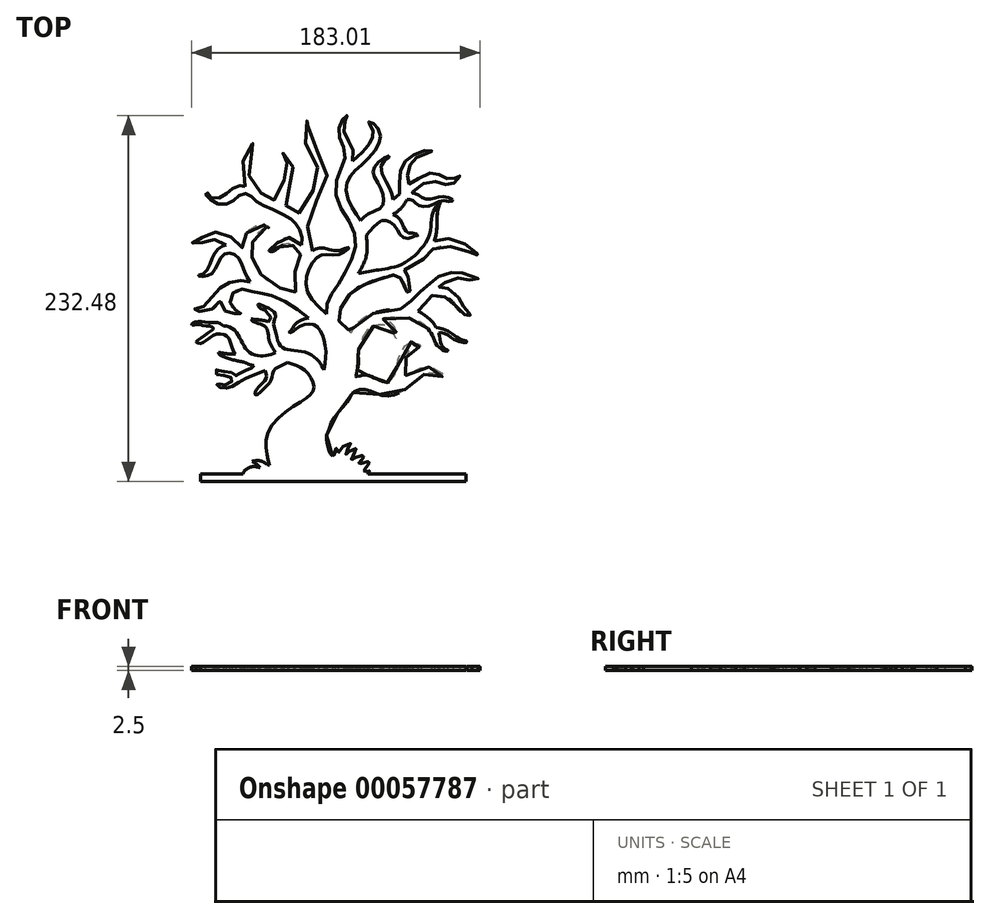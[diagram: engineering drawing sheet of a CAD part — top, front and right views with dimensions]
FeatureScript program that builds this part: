
annotation { "Feature Type Name" : "Feature", "Feature Type Description" : "" }
export const myFeature = defineFeature(function(context is Context, id is Id, definition is map)
    precondition{}
    {
        {
            var Q0;
            Q0=qCreatedBy(makeId("Top.planeOp"),FACE);
            var sketch = newSketch(context, id + "F0", { "sketchPlane" : qUnion([Q0])});
            skFitSpline(sketch, "E0", {"points": [v(-37.23, -92.22) * mm, v(-37.93, -89.5) * mm, v(-37.64, -70.07) * mm, v(-14, -49.38) * mm, v(-9.05, -42.86) * mm, v(-12.92, -33.47) * mm, v(-20.4, -28.62) * mm, v(-30.52, -26.33) * mm, v(-44.65, -28.9) * mm, v(-53.5, -26.46) * mm], "startDerivative": vector(-6.46, 28.02) * mm, "endDerivative": vector(-86.12, 39.68) * mm});
            skFitSpline(sketch, "E1", {"points": [v(-53.5, -26.46) * mm, v(-62.24, -24.53) * mm, v(-69.12, -21.43) * mm, v(-69.55, -20.32) * mm], "startDerivative": vector(-17.56, 2.77) * mm, "endDerivative": vector(-0.49, 6.57) * mm});
            skFitSpline(sketch, "E2", {"points": [v(-69.55, -20.32) * mm, v(-63.18, -21.35) * mm, v(-58.8, -21.52) * mm], "startDerivative": vector(12.15, -2.3) * mm, "endDerivative": vector(9.28, -0.04) * mm});
            skFitSpline(sketch, "E3", {"points": [v(-58.8, -21.52) * mm, v(-61.03, -17.47) * mm, v(-63.61, -10.67) * mm, v(-71.93, -9.08) * mm, v(-80.86, -14.69) * mm, v(-83.78, -13.74) * mm, v(-82.12, -12.32) * mm, v(-68.6, -3.79) * mm, v(-58.2, -7.58) * mm, v(-51.73, -18.6) * mm, v(-42.1, -22.64) * mm, v(-33.23, -20.57) * mm], "startDerivative": vector(-32.51, 46.9) * mm, "endDerivative": vector(77.44, 28.59) * mm});
            skFitSpline(sketch, "E4", {"points": [v(-33.23, -20.57) * mm, v(-37.27, -13.17) * mm, v(-39.86, -4.05) * mm, v(-47.76, -0.64) * mm, v(-48.83, 0.83) * mm], "startDerivative": vector(-16.8, 23.88) * mm, "endDerivative": vector(0.64, 6.3) * mm});
            skFitSpline(sketch, "E5", {"points": [v(-48.83, 0.83) * mm, v(-35.48, -2.55) * mm, v(-31.57, -14.02) * mm, v(-26.34, -18.5) * mm, v(-14.47, -20.28) * mm, v(-5.83, -26.09) * mm, v(-2.67, -31.48) * mm], "startDerivative": vector(73.32, -8.54) * mm, "endDerivative": vector(18.96, -39.09) * mm});
            skFitSpline(sketch, "E6", {"points": [v(-2.67, -31.48) * mm, v(-1.43, -19.6) * mm, v(-3.36, -10.05) * mm, v(-7.1, -3.92) * mm, v(-12.97, -2.37) * mm, v(-19.74, -4.89) * mm, v(-22.7, -7.34) * mm, v(-24.45, -7.73) * mm, v(-24.64, -7.2) * mm, v(-23.41, -6.37) * mm, v(-21.54, -3.28) * mm, v(-17.68, 0) * mm, v(-12.52, 1.37) * mm], "startDerivative": vector(16.4, 90.94) * mm, "endDerivative": vector(60.2, 10.33) * mm});
            skFitSpline(sketch, "E7", {"points": [v(-12.52, 1.37) * mm, v(-24.06, 10) * mm, v(-38, 16.41) * mm, v(-45.65, 17.78) * mm, v(-49.75, 18.87) * mm, v(-57.81, 19.42) * mm, v(-62.18, 13.68) * mm, v(-60.95, 8.35) * mm, v(-56.05, 5.43) * mm, v(-55.53, 4.23) * mm, v(-58.2, 4.23) * mm, v(-64.66, 5.34) * mm, v(-68.36, 11.89) * mm, v(-68.7, 12.49) * mm, v(-69.22, 12.32) * mm, v(-70.43, 10) * mm, v(-78.6, 5.6) * mm, v(-84.97, 6.9) * mm, v(-84.8, 7.24) * mm, v(-79.3, 8.79) * mm, v(-71.63, 17.4) * mm, v(-65, 22.99) * mm, v(-55.7, 25.14) * mm, v(-49.5, 24.45) * mm], "startDerivative": vector(-156.26, 128.1) * mm, "endDerivative": vector(126.07, -24.69) * mm});
            skFitSpline(sketch, "E8", {"points": [v(-49.5, 24.45) * mm, v(-52.85, 30.29) * mm, v(-56.83, 39.4) * mm, v(-61.9, 42.67) * mm, v(-66.9, 41.22) * mm, v(-70.51, 35) * mm, v(-73.99, 29.64) * mm, v(-78.7, 28.05) * mm, v(-82.24, 28.19) * mm, v(-82.31, 28.62) * mm, v(-81.95, 28.7) * mm, v(-78.9, 29.64) * mm, v(-74.78, 36.15) * mm, v(-72.25, 42.38) * mm, v(-67.83, 46.86) * mm, v(-64.72, 47.95) * mm], "startDerivative": vector(-43.88, 65.41) * mm, "endDerivative": vector(53.78, 11.6) * mm});
            skFitSpline(sketch, "E9", {"points": [v(-64.72, 47.95) * mm, v(-68.7, 50.12) * mm, v(-73.4, 51.28) * mm, v(-78.33, 50.27) * mm, v(-80.5, 49.18) * mm, v(-85.35, 48.96) * mm, v(-86.07, 49.1) * mm, v(-85.78, 49.61) * mm, v(-82.89, 50.92) * mm, v(-78.62, 53.81) * mm, v(-72.9, 55.91) * mm, v(-65.52, 54.75) * mm, v(-59.37, 50.84) * mm, v(-54.73, 46.28) * mm, v(-54.3, 46.5) * mm, v(-52.49, 53.96) * mm, v(-44.31, 60.4) * mm, v(-37.43, 59.68) * mm, v(-37.65, 59.1) * mm, v(-38.8, 59.24) * mm, v(-46.4, 53.02) * mm, v(-48.65, 44.48) * mm, v(-47.93, 38.47) * mm, v(-42.28, 28.99) * mm, v(-29.9, 20.37) * mm, v(-20.79, 17.84) * mm, v(-20.71, 18.06) * mm, v(-21.3, 28.26) * mm, v(-18.04, 39.84) * mm, v(-17.75, 42.6) * mm, v(-19.77, 45.63) * mm, v(-25.27, 48.67) * mm, v(-30.85, 46.65) * mm, v(-35.26, 43.75) * mm, v(-37.43, 44.19) * mm, v(-37.22, 44.55) * mm, v(-35.77, 45.34) * mm, v(-31.43, 50.34) * mm, v(-27.23, 52.58) * mm, v(-21.44, 51.71) * mm, v(-16.73, 47.95) * mm], "startDerivative": vector(-159.85, 95.28) * mm, "endDerivative": vector(153.51, -155.1) * mm});
            skFitSpline(sketch, "E10", {"points": [v(-16.73, 47.95) * mm, v(-16.73, 53.67) * mm, v(-19.41, 59.82) * mm, v(-21.8, 62.93) * mm, v(-27.3, 66.7) * mm, v(-38.3, 71.84) * mm, v(-45.4, 75.53) * mm, v(-48.58, 78.71) * mm, v(-52.78, 80.67) * mm, v(-57.48, 78.57) * mm, v(-61.97, 74.88) * mm, v(-68.63, 73.57) * mm, v(-75.36, 77.2) * mm, v(-77.68, 80.45) * mm, v(-76.66, 81.24) * mm, v(-76.45, 80.23) * mm, v(-72.76, 77.34) * mm, v(-65.37, 79.87) * mm, v(-60.52, 83.78) * mm, v(-54.95, 85.59) * mm, v(-52.63, 85.08) * mm], "startDerivative": vector(12.24, 106.84) * mm, "endDerivative": vector(59.66, -23.4) * mm});
            skFitSpline(sketch, "E11", {"points": [v(-52.63, 85.08) * mm, v(-54.59, 91.38) * mm, v(-53.72, 102.23) * mm, v(-50.25, 108.9) * mm, v(-47.86, 112) * mm, v(-47.86, 112.8) * mm, v(-47.5, 113.45) * mm, v(-46.63, 113.02) * mm, v(-46.77, 111.14) * mm, v(-47.93, 109.11) * mm, v(-50.25, 102.3) * mm, v(-50.17, 92.1) * mm, v(-47.06, 85.66) * mm, v(-42.72, 81.24) * mm, v(-41.78, 79.8) * mm, v(-35.77, 76.25) * mm, v(-34.32, 75.82) * mm, v(-34.25, 76.76) * mm, v(-31.79, 83.42) * mm, v(-28.17, 88.34) * mm, v(-25.27, 93.33) * mm, v(-25.2, 98.1) * mm, v(-27.23, 101.87) * mm, v(-29.11, 103.9) * mm, v(-29.62, 105.78) * mm, v(-29.26, 106.43) * mm, v(-28.53, 105.85) * mm, v(-28.82, 104.91) * mm, v(-26.72, 103.25) * mm, v(-22.16, 96.73) * mm, v(-21.94, 90) * mm, v(-24.7, 83.92) * mm, v(-27.37, 78.35) * mm, v(-27.37, 74.15) * mm, v(-26.65, 72.63) * mm, v(-22.81, 70.39) * mm, v(-18.76, 67.28) * mm, v(-18.69, 67.64) * mm, v(-12.97, 78.06) * mm, v(-9.93, 81.9) * mm, v(-6.38, 90) * mm, v(-6.31, 96.52) * mm, v(-11.09, 106) * mm, v(-14.63, 113.53) * mm, v(-15.5, 119.39) * mm, v(-13.4, 126.92) * mm, v(-11.81, 128.94) * mm, v(-11.23, 128.3) * mm, v(-11.74, 127.57) * mm, v(-12.82, 122) * mm, v(-10.44, 113.67) * mm, v(-5.3, 105.5) * mm, v(-1.03, 98.04) * mm, v(-1.53, 85.73) * mm, v(-5.95, 77.84) * mm, v(-12.32, 68.8) * mm, v(-12.82, 59.39) * mm, v(-10.87, 56.42) * mm, v(-9.93, 44.19) * mm], "startDerivative": vector(-120.08, 280.65) * mm, "endDerivative": vector(-5.28, -540.47) * mm});
            skFitSpline(sketch, "E12", {"points": [v(-9.93, 44.19) * mm, v(-7.69, 45.56) * mm, v(-3.85, 46.07) * mm, v(1.36, 44.9) * mm, v(7, 44.19) * mm, v(12.36, 46.21) * mm, v(13.3, 46.14) * mm, v(11.57, 44.19) * mm, v(5.7, 41.5) * mm, v(-2.26, 41.8) * mm, v(-7.18, 39.77) * mm, v(-12.68, 31.01) * mm, v(-13.26, 18.64) * mm, v(-1.03, 4.16) * mm], "startDerivative": vector(40.45, 30.37) * mm, "endDerivative": vector(114.16, -103.83) * mm});
            skFitSpline(sketch, "E13", {"points": [v(-1.03, 4.16) * mm, v(0, 12.2) * mm, v(5.27, 20.94) * mm, v(12.32, 33.52) * mm, v(17.54, 48.24) * mm, v(14.16, 61.43) * mm, v(5.88, 76.46) * mm, v(6.19, 92.1) * mm, v(10.8, 102.53) * mm, v(9.1, 112.04) * mm, v(6.65, 119.25) * mm, v(8.34, 126.15) * mm, v(10.94, 129.83) * mm, v(12.17, 129.99) * mm, v(10.8, 126.15) * mm, v(10.94, 117.72) * mm, v(15.24, 110.2) * mm, v(15.54, 101.3) * mm], "startDerivative": vector(2.52, 146.68) * mm, "endDerivative": vector(-17.17, -159.84) * mm});
            skFitSpline(sketch, "E14", {"points": [v(15.54, 101.3) * mm, v(20.45, 105.45) * mm, v(23.52, 108.67) * mm, v(27.05, 113.73) * mm, v(28.43, 120.94) * mm, v(25.97, 125.08) * mm, v(25.97, 126) * mm, v(29.8, 124.31) * mm, v(33.18, 117.1) * mm, v(29.96, 108.05) * mm, v(20, 97.62) * mm, v(13.86, 91.18) * mm, v(11.25, 83.36) * mm, v(15.54, 71.25) * mm, v(20.76, 63.27) * mm], "startDerivative": vector(77.02, 62.47) * mm, "endDerivative": vector(65.04, -83.73) * mm});
            skFitSpline(sketch, "E15", {"points": [v(20.76, 63.27) * mm, v(25.05, 67.26) * mm, v(33.95, 71.86) * mm, v(35.33, 76.61) * mm, v(33.34, 84.44) * mm, v(28.58, 93.33) * mm, v(31.19, 99.47) * mm, v(38.24, 104.37) * mm, v(39.01, 103.91) * mm, v(33.8, 98.85) * mm, v(38.86, 84.44) * mm, v(41.16, 76.61) * mm], "startDerivative": vector(41.17, 51.56) * mm, "endDerivative": vector(11.33, -71.84) * mm});
            skFitSpline(sketch, "E16", {"points": [v(41.16, 76.61) * mm, v(45.45, 80.6) * mm, v(45.29, 90.93) * mm, v(48.66, 100.29) * mm, v(54.18, 105.04) * mm, v(63.67, 108.12) * mm, v(65.97, 107.5) * mm, v(65.66, 107.04) * mm, v(59.09, 104.9) * mm, v(52.95, 99.98) * mm, v(50.5, 92.31) * mm, v(51.6, 86.62) * mm, v(60.83, 92.2) * mm, v(68.8, 93.27) * mm, v(74.16, 90.66) * mm, v(79.38, 89.9) * mm, v(83.36, 92.2) * mm, v(83.67, 91.89) * mm, v(79.68, 86.98) * mm, v(73.7, 86.37) * mm, v(64.96, 88.51) * mm, v(53.89, 81.83) * mm, v(50.2, 76.61) * mm, v(45.76, 70.63) * mm, v(41.16, 67.26) * mm], "startDerivative": vector(110.78, 80.65) * mm, "endDerivative": vector(-110.46, -69.26) * mm});
            skFitSpline(sketch, "E17", {"points": [v(41.16, 67.26) * mm, v(45.24, 64.63) * mm, v(47.07, 61.26) * mm, v(49.26, 57.16) * mm, v(51.45, 55.51) * mm, v(55.55, 55.33) * mm, v(57, 53.78) * mm, v(56.37, 53.6) * mm, v(55.28, 53.7) * mm, v(50.9, 52.05) * mm, v(46.89, 53.33) * mm, v(42.96, 59.07) * mm, v(38.4, 63.08) * mm, v(34.03, 63.27) * mm, v(28.92, 59.25) * mm, v(24.36, 54.06) * mm], "startDerivative": vector(63.37, -31.9) * mm, "endDerivative": vector(-49.93, -59.23) * mm});
            skFitSpline(sketch, "E18", {"points": [v(24.36, 54.06) * mm, v(24.36, 41.38) * mm, v(19.25, 29.8) * mm], "startDerivative": vector(2.56, -25.89) * mm, "endDerivative": vector(-12.77, -22.63) * mm});
            skFitSpline(sketch, "E19", {"points": [v(19.25, 29.8) * mm, v(27.1, 31.26) * mm, v(35.21, 32.53) * mm, v(48.07, 36.27) * mm, v(61.84, 49.13) * mm, v(65.3, 59.07) * mm, v(66.22, 67.19) * mm, v(70.78, 74.76) * mm, v(71.14, 74.76) * mm, v(69.96, 71.47) * mm, v(69.14, 61.17) * mm, v(68.68, 54.97) * mm, v(67.5, 50.32) * mm], "startDerivative": vector(92.84, 17.97) * mm, "endDerivative": vector(-20.5, -69.36) * mm});
            skFitSpline(sketch, "E20", {"points": [v(67.5, 50.32) * mm, v(73.24, 51.87) * mm, v(83.73, 50.32) * mm, v(89.93, 45.85) * mm, v(95.13, 42.66) * mm, v(96.22, 42.38) * mm, v(96.22, 41.65) * mm, v(94.76, 41.56) * mm, v(94.58, 40.92) * mm, v(93.21, 41.47) * mm, v(84.73, 45.4) * mm, v(71.05, 46.76) * mm, v(64.94, 44.02) * mm, v(60.66, 38.92) * mm, v(48.17, 31.66) * mm, v(47.97, 31.21) * mm, v(49.1, 30.12) * mm, v(51.78, 24.65) * mm, v(52.02, 18.07) * mm, v(51.94, 16.29) * mm, v(50.88, 16.45) * mm, v(49.18, 23.11) * mm, v(44.38, 27.82) * mm, v(42.27, 28.31) * mm, v(41.78, 28.72) * mm, v(39.35, 28.15) * mm, v(28.54, 24.98) * mm, v(21.96, 22.14) * mm, v(13.75, 16.53) * mm, v(8.47, 8.57) * mm, v(6.93, 3.45) * mm, v(7.25, -1.34) * mm, v(12.21, -5.16) * mm, v(14.4, -7.84) * mm, v(14.9, -7.36) * mm, v(22.37, 1.34) * mm, v(46.09, 7.27) * mm], "startDerivative": vector(168, 66.2) * mm, "endDerivative": vector(398.56, 17.42) * mm});
            skFitSpline(sketch, "E21", {"points": [v(46.09, 7.27) * mm, v(52.9, 12.63) * mm, v(59.47, 18.84) * mm, v(65.07, 23.59) * mm, v(69.81, 27.6) * mm, v(78.33, 30.4) * mm, v(84.54, 30.04) * mm, v(89.05, 29.07) * mm, v(92.58, 27.24) * mm, v(95.25, 26.75) * mm, v(94.65, 25.78) * mm, v(88.56, 26.02) * mm, v(82.1, 26.88) * mm, v(73.22, 23.59) * mm, v(70.79, 22.14) * mm, v(70.66, 21.03) * mm, v(75.05, 20.67) * mm, v(82.47, 14.95) * mm, v(85.64, 9.71) * mm, v(87.34, 6.91) * mm, v(90.26, 4.33) * mm, v(91.36, 4.33) * mm, v(90.38, 3.26) * mm, v(89.17, 2.65) * mm, v(87.34, 3.14) * mm, v(82.72, 6.91) * mm, v(76.26, 13.97) * mm, v(66.65, 15.92) * mm, v(64.94, 15.19) * mm, v(58.86, 7.27) * mm, v(57.15, 5.94) * mm], "startDerivative": vector(152.87, 113.18) * mm, "endDerivative": vector(-62.21, -32.26) * mm});
            skFitSpline(sketch, "E22", {"points": [v(57.15, 5.94) * mm, v(61.99, 2.85) * mm, v(67.5, -2.44) * mm, v(68.41, -4.26) * mm, v(71.56, -5.08) * mm, v(78.86, -8.46) * mm, v(84.92, -12.6) * mm, v(88.02, -13.15) * mm, v(88.02, -13.88) * mm, v(86.47, -14.2) * mm, v(79.81, -12.1) * mm, v(76.17, -9.41) * mm, v(71.74, -7.77) * mm, v(70.33, -8.1) * mm, v(70.33, -8.46) * mm, v(71.56, -14.02) * mm, v(73.34, -17.4) * mm, v(75.94, -18.94) * mm, v(76.08, -19.3) * mm, v(74.89, -19.63) * mm, v(72.56, -18.62) * mm, v(68.6, -14.93) * mm, v(66.32, -9.78) * mm, v(63.44, -5.31) * mm, v(59.66, -1.9) * mm, v(52.55, 1.2) * mm, v(39.76, 1.72) * mm, v(35.05, 1) * mm, v(39.45, -1.25) * mm, v(42.21, -4.94) * mm, v(43.75, -9.95) * mm, v(43.24, -11.59) * mm, v(42.72, -11.18) * mm, v(42.72, -10.26) * mm, v(37.5, -3.91) * mm, v(32.08, -2.89) * mm, v(25.32, -5.86) * mm, v(19.7, -17.12) * mm, v(19.18, -22.95) * mm, v(19.28, -27.56) * mm, v(17.65, -35.13) * mm, v(17.54, -35.75) * mm, v(23.38, -34.72) * mm, v(29.21, -36.57) * mm, v(35.87, -39.12) * mm, v(39.04, -39.02) * mm, v(43.34, -32.68) * mm, v(43.65, -30.22) * mm, v(47.33, -17.83) * mm, v(54.3, -13.43) * mm, v(57.62, -15.17) * mm, v(59.4, -16.4) * mm, v(57.62, -16.8) * mm, v(54.8, -16.3) * mm, v(50.5, -20.4) * mm, v(49.28, -28.48) * mm, v(49.38, -33.29) * mm, v(49.17, -34.93) * mm, v(50.7, -34.21) * mm, v(60.23, -29.8) * mm, v(70.67, -32.27) * mm, v(73.74, -35.75) * mm, v(72.61, -35.75) * mm, v(69.65, -34.1) * mm, v(63.1, -33.7) * mm, v(58.8, -35.64) * mm, v(51.63, -41.89) * mm, v(45.9, -45.78) * mm, v(35.35, -47.93) * mm, v(23.79, -43.83) * mm, v(15.5, -46.29) * mm, v(12.53, -51.2) * mm, v(3.72, -62.16) * mm, v(0, -70.45) * mm, v(-0.97, -74.78) * mm, v(1.22, -84.1) * mm, v(2.74, -86.23) * mm], "startDerivative": vector(316.06, -183.06) * mm, "endDerivative": vector(154.23, -155.5) * mm});
            skFitSpline(sketch, "E23", {"points": [v(-37.23, -92.22) * mm, v(-42.9, -89.27) * mm, v(-48.15, -89.53) * mm], "startDerivative": vector(-10.66, 5.99) * mm, "endDerivative": vector(-10.92, -1.79) * mm});
            skFitSpline(sketch, "E24", {"points": [v(-48.15, -89.53) * mm, v(-44.28, -92.2) * mm, v(-43.24, -93.49) * mm], "startDerivative": vector(7.24, -4.5) * mm, "endDerivative": vector(2.14, -3.32) * mm});
            skFitSpline(sketch, "E25", {"points": [v(-43.24, -93.49) * mm, v(-48.32, -93.02) * mm, v(-53.03, -95.51) * mm, v(-53.92, -97.56) * mm], "startDerivative": vector(-13.25, 3.2) * mm, "endDerivative": vector(-1.8, -8.27) * mm});
            skFitSpline(sketch, "E26", {"points": [v(-53.92, -97.56) * mm, v(-51.05, -96.88) * mm, v(-46.37, -97.56) * mm], "startDerivative": vector(6.09, 2.16) * mm, "endDerivative": vector(8.9, -2) * mm});
            skLineSegment(sketch, "E27", {"start": v(-46.37, -97.56) * mm, "end": v(-46.37, -97.56) * mm});
            skLineSegment(sketch, "E28", {"start": v(-84.8, 7.24) * mm, "end": v(-85.32, 24.31) * mm, "construction": true});
            skLineSegment(sketch, "E29", {"start": v(-85.32, 24.31) * mm, "end": v(91.36, 4.33) * mm, "construction": true});
            skFitSpline(sketch, "E30", {"points": [v(70.33, -8.1) * mm, v(68.72, -8.1) * mm, v(66.26, -7.43) * mm, v(63.44, -5.31) * mm], "startDerivative": vector(-5.7, -0.28) * mm, "endDerivative": vector(-6.95, 6.19) * mm});
            skFitSpline(sketch, "E31", {"points": [v(-34.41, -4.06) * mm, v(-34.29, 0) * mm, v(-33.2, 2.67) * mm, v(-35.78, 6.6) * mm, v(-41.56, 9.35) * mm, v(-44.25, 10.34) * mm, v(-44.5, 10) * mm, v(-43.16, 7.66) * mm, v(-39.92, 6.36) * mm, v(-38.47, 4.42) * mm, v(-36.48, 1.98) * mm, v(-37.97, -0.91) * mm], "startDerivative": vector(-4.06, 42.22) * mm, "endDerivative": vector(-27.8, -32.84) * mm});
            skFitSpline(sketch, "E32", {"points": [v(-66.39, -3.5) * mm, v(-69.47, -1.64) * mm, v(-75.72, -1.33) * mm, v(-83.78, -0.85) * mm, v(-86.63, -2.43) * mm, v(-86.16, -2.9) * mm, v(-82.76, -2.51) * mm, v(-79.75, -3.15) * mm, v(-73.11, -4.41) * mm, v(-73.18, -5.8) * mm], "startDerivative": vector(-25.1, 20.7) * mm, "endDerivative": vector(-9.63, -22.76) * mm});
            skFitSpline(sketch, "E33", {"points": [v(-28.41, -26.35) * mm, v(-37.58, -30.63) * mm, v(-44.34, -33.71) * mm, v(-52.48, -37.04) * mm, v(-60.53, -41.8) * mm, v(-66.41, -43.07) * mm, v(-70.63, -41.1) * mm, v(-69.94, -40.13) * mm, v(-67.5, -41.1) * mm, v(-60.83, -38.27) * mm, v(-63.57, -35.23) * mm, v(-71.2, -33.79) * mm, v(-70.33, -30.85) * mm, v(-69.25, -32.02) * mm, v(-61.9, -32.87) * mm, v(-58.08, -35.13) * mm, v(-54.83, -32.73) * mm, v(-48.07, -30.18) * mm, v(-46.87, -28.77) * mm], "startDerivative": vector(-105.13, -29.15) * mm, "endDerivative": vector(29.74, 40.47) * mm});
            skLineSegment(sketch, "E34", {"start": v(25.38, -97.56) * mm, "end": v(87.75, -97.56) * mm});
            skLineSegment(sketch, "E35", {"start": v(87.75, -97.56) * mm, "end": v(87.75, -102.35) * mm});
            skLineSegment(sketch, "E36", {"start": v(87.75, -102.35) * mm, "end": v(-81.07, -102.35) * mm});
            skLineSegment(sketch, "E37", {"start": v(-81.07, -102.35) * mm, "end": v(-81.07, -97.56) * mm});
            skLineSegment(sketch, "E38", {"start": v(-81.07, -97.56) * mm, "end": v(-46.37, -97.56) * mm});
            skFitSpline(sketch, "E39", {"points": [v(2.74, -86.23) * mm, v(3.57, -86.66) * mm, v(4.11, -84.1) * mm, v(5.53, -80.54) * mm, v(5.63, -81.32) * mm, v(6.37, -84.1) * mm, v(8.42, -81.08) * mm, v(14.45, -78.38) * mm, v(12.3, -81.57) * mm, v(11.41, -85.24) * mm, v(13.96, -82.74) * mm, v(18.08, -81.57) * mm, v(16.17, -84.8) * mm, v(14.85, -88.77) * mm, v(18.23, -86.23) * mm, v(23.08, -86.23) * mm, v(20.82, -88.53) * mm, v(19.45, -91.56) * mm, v(23.18, -90.04) * mm, v(26.7, -90.2) * mm, v(24.06, -93.08) * mm, v(22.74, -96.42) * mm, v(24.16, -95.63) * mm, v(26.17, -95.48) * mm, v(25.48, -96.8) * mm, v(25.38, -97.56) * mm], "startDerivative": vector(43.65, -35.45) * mm, "endDerivative": vector(4.37, -33.58) * mm});
            skFitSpline(sketch, "E40", {"points": [v(-25.76, -26.76) * mm, v(-31, -29.27) * mm, v(-34.93, -32.5) * mm, v(-35.97, -37.6) * mm, v(-39.9, -42.45) * mm, v(-45.8, -47.53) * mm, v(-45.91, -44.88) * mm, v(-40.83, -38.98) * mm, v(-39.2, -35.86) * mm, v(-39.98, -31.83) * mm], "startDerivative": vector(-45.07, -20.48) * mm, "endDerivative": vector(-15.86, 43.29) * mm});
            skFitSpline(sketch, "E41", {"points": [v(61.84, 49.13) * mm, v(65.02, 50.52) * mm, v(67.5, 50.32) * mm], "startDerivative": vector(6, 3.37) * mm, "endDerivative": vector(5.3, -1.12) * mm});
            skFitSpline(sketch, "E42", {"points": [v(19.25, 29.8) * mm, v(27.1, 31.26) * mm, v(35.21, 32.53) * mm, v(48.07, 36.27) * mm, v(61.84, 49.13) * mm, v(65.3, 59.07) * mm, v(66.22, 67.19) * mm, v(70.78, 74.76) * mm, v(71.14, 74.76) * mm, v(69.96, 71.47) * mm, v(69.14, 61.17) * mm, v(68.68, 54.97) * mm, v(67.5, 50.32) * mm], "startDerivative": vector(92.84, 17.97) * mm, "endDerivative": vector(-20.5, -69.36) * mm, "construction": true});
            skFitSpline(sketch, "E43", {"points": [v(50.2, 76.61) * mm, v(53.14, 76.61) * mm, v(56.3, 73.83) * mm, v(63.42, 72.53) * mm, v(72.48, 75.93) * mm, v(78.64, 75.61) * mm, v(79.12, 76.61) * mm, v(72.57, 78.6) * mm, v(67.14, 77.55) * mm, v(60.9, 77.4) * mm, v(56.05, 80.3) * mm, v(53.54, 80.95) * mm, v(53.89, 81.83) * mm], "startDerivative": vector(47.35, 9.13) * mm, "endDerivative": vector(27.39, 47.5) * mm});
            skSolve(sketch);
        }
        {
            var Q0;
            Q0 = qSketchRegion(id + "F0", true);
            extrude(context, id + "F1", {"entities" : qUnion([Q0]), "depth" : 2.5 * mm});
        }
    });
